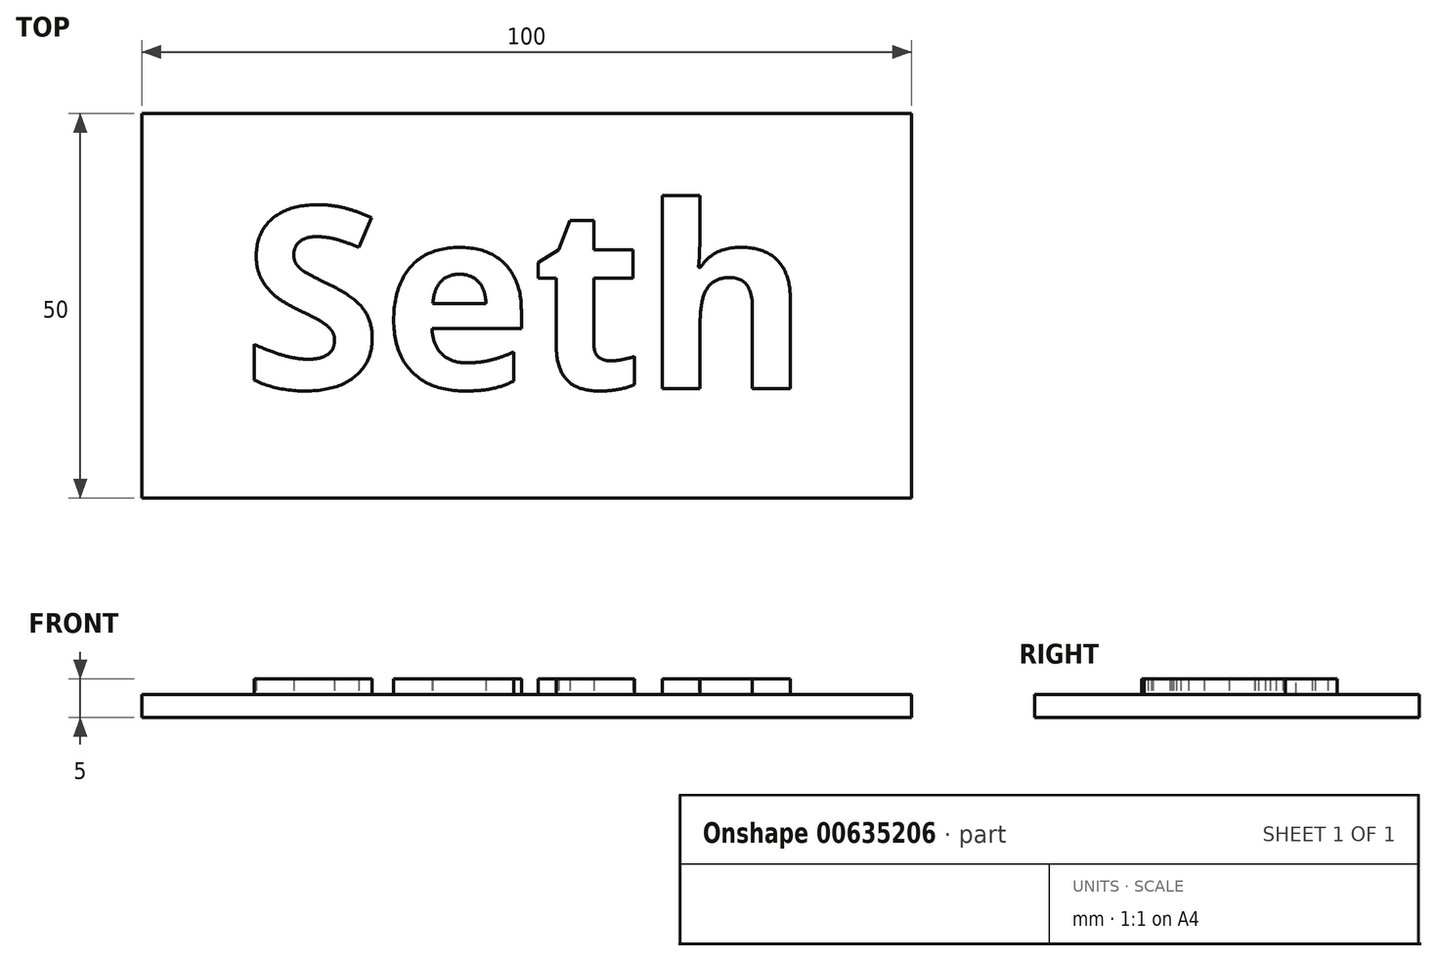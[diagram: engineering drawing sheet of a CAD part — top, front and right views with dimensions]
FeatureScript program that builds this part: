
annotation { "Feature Type Name" : "Feature", "Feature Type Description" : "" }
export const myFeature = defineFeature(function(context is Context, id is Id, definition is map)
    precondition{}
    {
        {
            var Q0;
            Q0=qCreatedBy(makeId("Top.planeOp"),FACE);
            var sketch = newSketch(context, id + "F0", { "sketchPlane" : qUnion([Q0])});
            skLineSegment(sketch, "E0.bottom", {"start": v(0, 0) * mm, "end": v(-100, 0) * mm});
            skLineSegment(sketch, "E0.top", {"start": v(0, 50) * mm, "end": v(-100, 50) * mm});
            skLineSegment(sketch, "E0.left", {"start": v(0, 0) * mm, "end": v(0, 50) * mm});
            skLineSegment(sketch, "E0.right", {"start": v(-100, 0) * mm, "end": v(-100, 50) * mm});
            skSolve(sketch);
        }
        {
            var Q0;
            Q0 = qSketchRegion(id + "F0", true);
            extrude(context, id + "F1", {"entities" : qUnion([Q0]), "depth" : 3 * mm, "offsetDistance" : 25 * mm});
        }
        {
            var Q0;
            Q0=makeQuery(id+"F1.opExtrude","CAP_FACE",FACE,{"disambiguationData":[OSD([sQuery(id+"F0.wireOp",EDGE,"E0.bottom"),sQuery(id+"F0.wireOp",EDGE,"E0.top"),sQuery(id+"F0.wireOp",EDGE,"E0.left"),sQuery(id+"F0.wireOp",EDGE,"E0.right")])],"isStart":false});
            var sketch = newSketch(context, id + "F2", { "sketchPlane" : qUnion([Q0])});
            skText(sketch, "E1", { "text": "Seth", "fontName": "OpenSans-Bold.ttf"});
            const initialGuessF2  = {"E1": [-0.08693, 0.01425, 1, 0, 0.02375]};
            skSetInitialGuess(sketch, initialGuessF2);
            skSolve(sketch);
        }
        {
            var Q0;
            Q0 = qSketchRegion(id + "F2", true);
            extrude(context, id + "F3", {"entities" : qUnion([Q0]), "operationType" : NewBodyOperationType.ADD, "depth" : 2 * mm, "offsetDistance" : 25 * mm});
        }
    });
